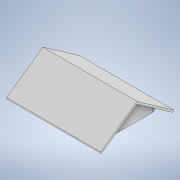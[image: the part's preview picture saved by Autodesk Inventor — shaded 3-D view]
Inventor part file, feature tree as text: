
AUTODESK INVENTOR PART (.ipt)
format: ipt  version: 2021 (Build 250183000, 183)  size: 196,096 bytes
history: native  units: mm
features: extrude x6, sketch x6, projected_geometry x6
ambient origin geometry x8: Origin, YZ Plane, XZ Plane, XY Plane, X Axis, Y Axis, Z Axis, Center Point
bodies: Volumenkörper1 (feature_tree)
feature tree (18):
  extrude  "Extrusion1"  Depth=49.0mm
  extrude  "Extrusion2"  Depth=2.0mm TaperAngle=0.0deg
  extrude  "Extrusion3"  Depth=2.0mm
  extrude  "Extrusion4"  Depth=80.0mm TaperAngle=0.0deg
  extrude  "Extrusion5"  Depth=34.0mm
  extrude  "Extrusion6"  Depth=2.0mm TaperAngle=0.0deg
  sketch  "Skizze1"  dims[d0=67.0mm d1=49.0mm]
  sketch  "Skizze2"  dims[d2=5.0mm d3=2.0mm d4=0.0mm]
  projected_geometry  "Projizierte Kontur1"
  projected_geometry  "Projizierte Kontur2"
  projected_geometry  "Projizierte Kontur3"
  sketch  "Skizze3"  dims[d5=6.108652mm d7=2.0mm]
  projected_geometry  "Projizierte Kontur4"
  sketch  "Skizze4"  dims[d8=2.0mm d9=80.0mm d10=0.0mm]
  projected_geometry  "Projizierte Kontur5"
  sketch  "Skizze5"  dims[d11=80.0mm d12=0.0mm d13=34.0mm]
  sketch  "Skizze6"  dims[d14=52.0mm d15=2.0mm d16=0.0mm d17=30.0mm d18=5.0mm d19=0.0mm d20=0.5mm d21=0.0mm d22=0.0mm d23=2.0mm d24=2.0mm]
  projected_geometry  "Projizierte Kontur6"
